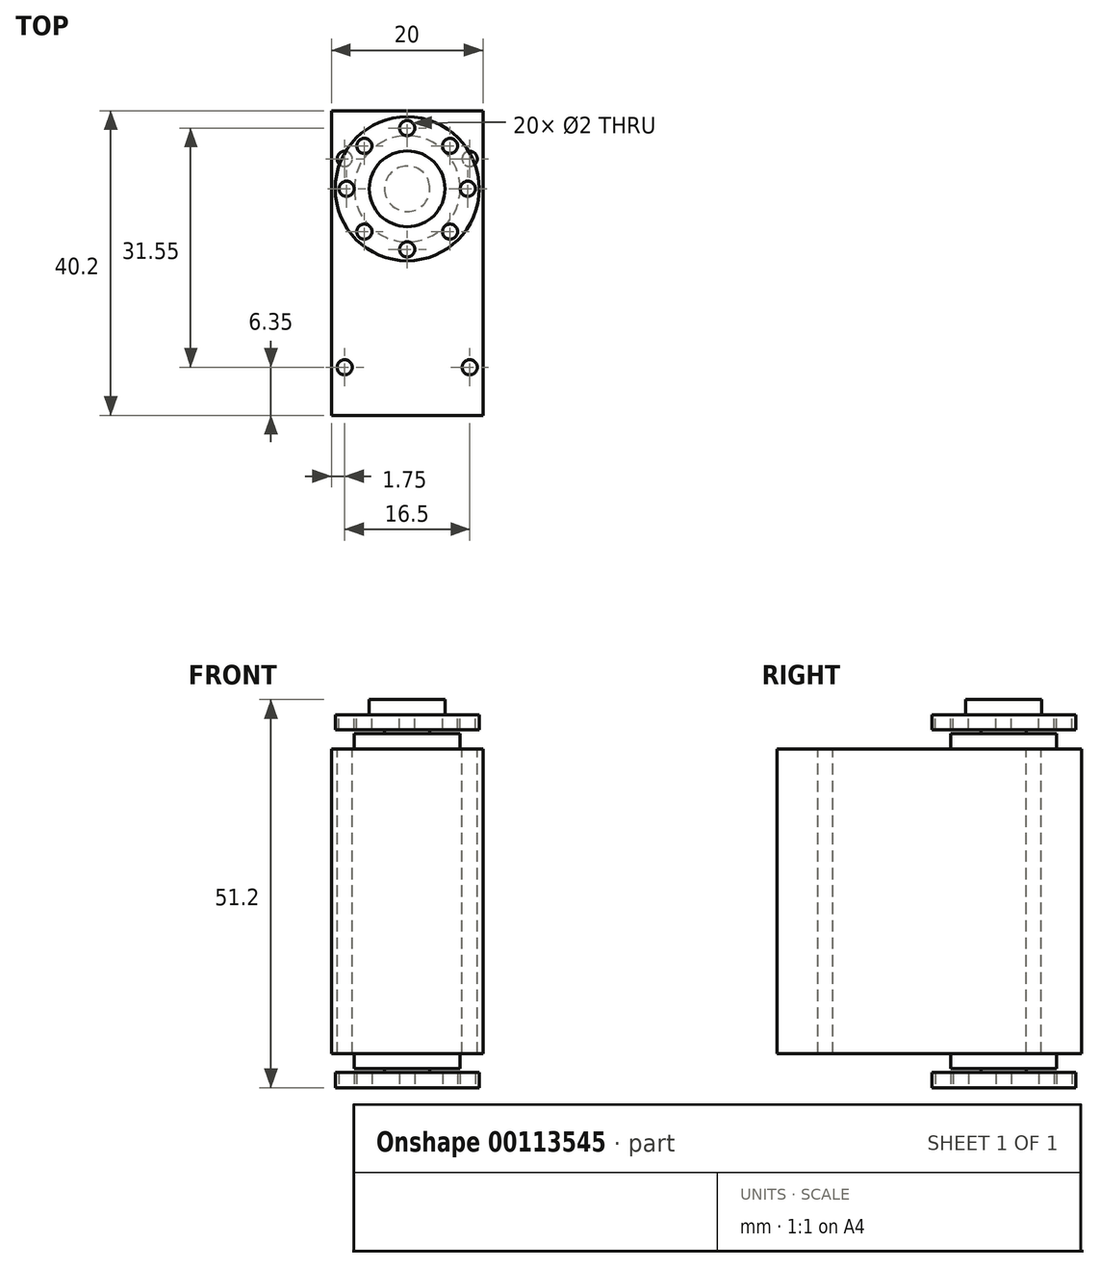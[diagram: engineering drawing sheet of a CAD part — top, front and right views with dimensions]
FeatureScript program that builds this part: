
annotation { "Feature Type Name" : "Feature", "Feature Type Description" : "" }
export const myFeature = defineFeature(function(context is Context, id is Id, definition is map)
    precondition{}
    {
        {
            var Q0;
            Q0=qCreatedBy(makeId("Top.planeOp"),FACE);
            var sketch = newSketch(context, id + "F0", { "sketchPlane" : qUnion([Q0])});
            skLineSegment(sketch, "E0.bottom", {"start": v(0, 0) * mm, "end": v(20, 0) * mm});
            skLineSegment(sketch, "E0.top", {"start": v(0, 40.2) * mm, "end": v(20, 40.2) * mm});
            skLineSegment(sketch, "E0.left", {"start": v(0, 0) * mm, "end": v(0, 40.2) * mm});
            skLineSegment(sketch, "E0.right", {"start": v(20, 0) * mm, "end": v(20, 40.2) * mm});
            skSolve(sketch);
        }
        {
            var Q0;
            Q0=qSketchRegion(id+"F0",true);
            extrude(context, id + "F1", {"entities" : qUnion([Q0]), "depth" : 40.2 * mm});
        }
        {
            var Q0;
            Q0=makeQuery(id+"F1.opExtrude","CAP_FACE",FACE,{"disambiguationData":[OSD([sQuery(id+"F0.wireOp",EDGE,"E0.bottom"),sQuery(id+"F0.wireOp",EDGE,"E0.top"),sQuery(id+"F0.wireOp",EDGE,"E0.left"),sQuery(id+"F0.wireOp",EDGE,"E0.right")])],"isStart":false});
            var sketch = newSketch(context, id + "F2", { "sketchPlane" : qUnion([Q0])});
            skLineSegment(sketch, "E1", {"start": v(10, 40.2) * mm, "end": v(10, 0) * mm, "construction": true});
            skLineSegment(sketch, "E2", {"start": v(0, 20.1) * mm, "end": v(20, 20.1) * mm, "construction": true});
            skCircle(sketch, "E3", {"center": v(1.75, 33.85) * mm, "radius": 1 * mm});
            skCircle(sketch, "E4.MirrorC", {"center": v(18.25, 33.85) * mm, "radius": 1 * mm});
            skCircle(sketch, "E5.MirrorC", {"center": v(1.75, 6.35) * mm, "radius": 1 * mm});
            skCircle(sketch, "E6.MirrorC", {"center": v(18.25, 6.35) * mm, "radius": 1 * mm});
            skSolve(sketch);
        }
        {
            var Q0;
            Q0=qSketchRegion(id+"F2",true);
            extrude(context, id + "F3", {"entities" : qUnion([Q0]), "operationType" : NewBodyOperationType.REMOVE, "endBound" : BoundingType.THROUGH_ALL, "oppositeDirection" : true, "depth" : 25 * mm});
        }
        {
            var Q0;
            Q0=makeQuery(id+"F1.opExtrude","CAP_FACE",FACE,{"disambiguationData":[OSD([sQuery(id+"F0.wireOp",EDGE,"E0.bottom"),sQuery(id+"F0.wireOp",EDGE,"E0.top"),sQuery(id+"F0.wireOp",EDGE,"E0.left"),sQuery(id+"F0.wireOp",EDGE,"E0.right")])],"isStart":false});
            var sketch = newSketch(context, id + "F4", { "sketchPlane" : qUnion([Q0])});
            skCircle(sketch, "E7", {"center": v(10, 29.9) * mm, "radius": 7 * mm});
            skLineSegment(sketch, "E8", {"start": v(0, 20.1) * mm, "end": v(20, 20.1) * mm, "construction": true});
            skSolve(sketch);
        }
        {
            var Q0;
            Q0=qSketchRegion(id+"F4",true);
            extrude(context, id + "F5", {"entities" : qUnion([Q0]), "operationType" : NewBodyOperationType.ADD, "depth" : 2 * mm, "hasSecondDirection" : true, "secondDirectionOppositeDirection" : true, "secondDirectionDepth" : (40.2 + 2) * mm});
        }
        {
            var Q0;
            Q0=makeQuery(id+"F5.opExtrude","CAP_FACE",FACE,{"disambiguationData":[OSD([sQuery(id+"F4.wireOp",EDGE,"E7")])],"isStart":false});
            var sketch = newSketch(context, id + "F6", { "sketchPlane" : qUnion([Q0])});
            skCircle(sketch, "E9", {"center": v(10, 29.9) * mm, "radius": 3 * mm});
            skSolve(sketch);
        }
        {
            var Q0;
            Q0=qSketchRegion(id+"F6",true);
            extrude(context, id + "F7", {"entities" : qUnion([Q0]), "operationType" : NewBodyOperationType.ADD, "depth" : 2.5 * mm});
        }
        {
            var Q0;
            Q0=makeQuery(id+"F7.opExtrude","CAP_FACE",FACE,{"disambiguationData":[OSD([sQuery(id+"F6.wireOp",EDGE,"E9")])],"isStart":false});
            var sketch = newSketch(context, id + "F8", { "sketchPlane" : qUnion([Q0])});
            skCircle(sketch, "E10", {"center": v(10, 29.9) * mm, "radius": 9.5 * mm});
            skCircle(sketch, "E11", {"center": v(10, 29.9) * mm, "radius": 8 * mm, "construction": true});
            skCircle(sketch, "E12", {"center": v(10, 37.9) * mm, "radius": 1 * mm});
            skCircle(sketch, "E13.1.0", {"center": v(4.34, 35.56) * mm, "radius": 1 * mm});
            skCircle(sketch, "E13.2.0", {"center": v(2, 29.9) * mm, "radius": 1 * mm});
            skCircle(sketch, "E13.3.0", {"center": v(4.34, 24.24) * mm, "radius": 1 * mm});
            skCircle(sketch, "E13.4.0", {"center": v(10, 21.9) * mm, "radius": 1 * mm});
            skCircle(sketch, "E13.5.0", {"center": v(15.66, 24.24) * mm, "radius": 1 * mm});
            skCircle(sketch, "E13.6.0", {"center": v(18, 29.9) * mm, "radius": 1 * mm});
            skCircle(sketch, "E13.7.0", {"center": v(15.66, 35.56) * mm, "radius": 1 * mm});
            skSolve(sketch);
        }
        {
            var Q0;
            Q0=qSketchRegion(id+"F8",true);
            extrude(context, id + "F9", {"entities" : qUnion([Q0]), "operationType" : NewBodyOperationType.ADD, "oppositeDirection" : true, "depth" : 2 * mm});
        }
        {
            var Q0;
            Q0=qCreatedBy(makeId("Top.planeOp"),FACE);
            cPlane(context, id + "F10", {"entities" : qUnion([Q0]), "cplaneType" : CPlaneType.OFFSET, "offset" : (40.2 / 2) * mm, "width" : 150 * mm, "height" : 150 * mm});
        }
        {
            var Q0;
            Q0=makeQuery(id+"F9.opExtrude","SWEPT_BODY",BODY,{"disambiguationData":[OSD([sQuery(id+"F8.wireOp",EDGE,"E10"),sQuery(id+"F8.wireOp",EDGE,"E12"),sQuery(id+"F8.wireOp",EDGE,"E13.1.0"),sQuery(id+"F8.wireOp",EDGE,"E13.2.0"),sQuery(id+"F8.wireOp",EDGE,"E13.3.0"),sQuery(id+"F8.wireOp",EDGE,"E13.4.0"),sQuery(id+"F8.wireOp",EDGE,"E13.5.0"),sQuery(id+"F8.wireOp",EDGE,"E13.6.0"),sQuery(id+"F8.wireOp",EDGE,"E13.7.0")])]});
            var Q1;
            Q1=makeQuery(id+"F1.opExtrude","SWEPT_BODY",BODY,{"disambiguationData":[OSD([sQuery(id+"F0.wireOp",EDGE,"E0.bottom"),sQuery(id+"F0.wireOp",EDGE,"E0.top"),sQuery(id+"F0.wireOp",EDGE,"E0.left"),sQuery(id+"F0.wireOp",EDGE,"E0.right")])]});
            var Q2;
            Q2=qCreatedBy(id+"F10.planeOp",FACE);
            mirror(context, id + "F11", {"operationType" : NewBodyOperationType.ADD, "entities" : qUnion([Q0, Q1]), "mirrorPlane" : qUnion([Q2])});
        }
        {
            var Q0;
            Q0=makeQuery(id+"F9.boolean.opBoolean","MERGE",FACE,{"derivedFrom":[makeQuery(id+"F7.opExtrude","CAP_FACE",FACE,{"disambiguationData":[OSD([sQuery(id+"F6.wireOp",EDGE,"E9")])],"isStart":false}),makeQuery(id+"F9.opExtrude","CAP_FACE",FACE,{"disambiguationData":[OSD([sQuery(id+"F8.wireOp",EDGE,"E10"),sQuery(id+"F8.wireOp",EDGE,"E12"),sQuery(id+"F8.wireOp",EDGE,"E13.1.0"),sQuery(id+"F8.wireOp",EDGE,"E13.2.0"),sQuery(id+"F8.wireOp",EDGE,"E13.3.0"),sQuery(id+"F8.wireOp",EDGE,"E13.4.0"),sQuery(id+"F8.wireOp",EDGE,"E13.5.0"),sQuery(id+"F8.wireOp",EDGE,"E13.6.0"),sQuery(id+"F8.wireOp",EDGE,"E13.7.0")])],"isStart":true})]});
            var sketch = newSketch(context, id + "F12", { "sketchPlane" : qUnion([Q0])});
            skCircle(sketch, "E14", {"center": v(10, 29.9) * mm, "radius": 5 * mm});
            skSolve(sketch);
        }
        {
            var Q0;
            Q0=qSketchRegion(id+"F12",true);
            extrude(context, id + "F13", {"entities" : qUnion([Q0]), "operationType" : NewBodyOperationType.ADD, "depth" : 2 * mm});
        }
    });
